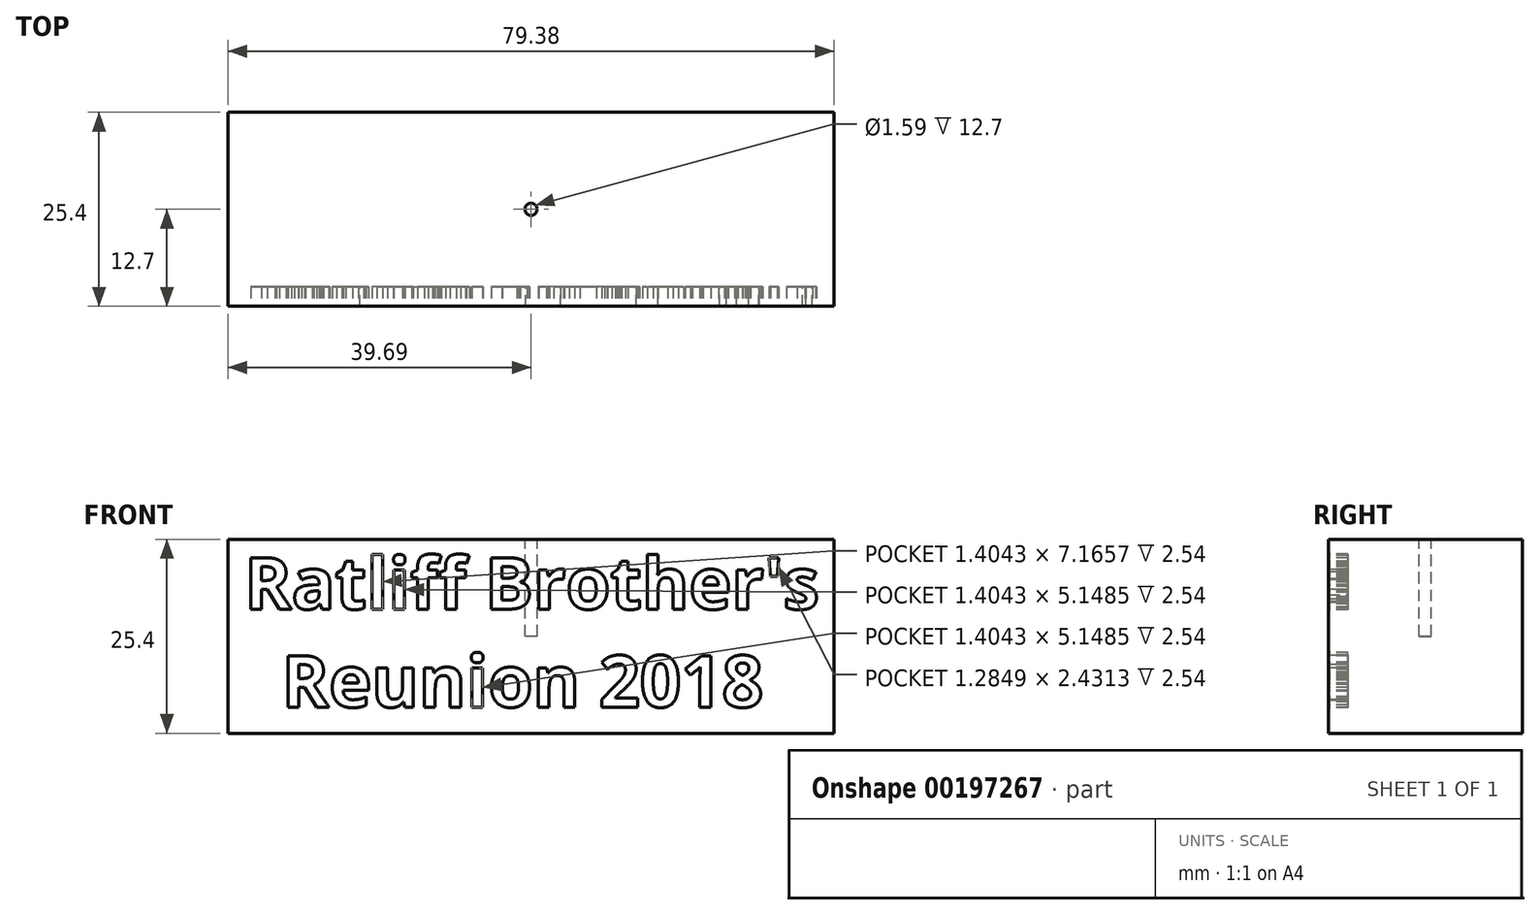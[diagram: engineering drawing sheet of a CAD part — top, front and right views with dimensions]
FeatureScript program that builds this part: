
annotation { "Feature Type Name" : "Feature", "Feature Type Description" : "" }
export const myFeature = defineFeature(function(context is Context, id is Id, definition is map)
    precondition{}
    {
        {
            var Q0;
            Q0=qCreatedBy(makeId("Top.planeOp"),FACE);
            var sketch = newSketch(context, id + "F0", { "sketchPlane" : qUnion([Q0])});
            skLineSegment(sketch, "E0.bottom", {"start": v(39.69, 12.7) * mm, "end": v(-39.69, 12.7) * mm});
            skLineSegment(sketch, "E0.top", {"start": v(39.69, -12.7) * mm, "end": v(-39.69, -12.7) * mm});
            skLineSegment(sketch, "E0.left", {"start": v(39.69, 12.7) * mm, "end": v(39.69, -12.7) * mm});
            skLineSegment(sketch, "E0.right", {"start": v(-39.69, 12.7) * mm, "end": v(-39.69, -12.7) * mm});
            skPoint(sketch, "E0.middle", {"position": v(0, 0) * mm});
            skSolve(sketch);
        }
        {
            var Q0;
            Q0=makeQuery(id+"F0.imprint","IMPRINT",FACE,{"disambiguationData":[TD([[makeQuery(id+"F0.imprint","IMPRINT",EDGE,{"derivedFrom":sQuery(id+"F0.wireOp",EDGE,"E0.bottom")}),1.0]])]});
            extrude(context, id + "F1", {"entities" : qUnion([Q0]), "endBound" : BoundingType.SYMMETRIC, "depth" : 25.4 * mm});
        }
        {
            var Q0;
            Q0=makeQuery(id+"F1.opExtrude","SWEPT_FACE",FACE,{"disambiguationData":[OSD([sQuery(id+"F0.wireOp",EDGE,"E0.top")])]});
            var sketch = newSketch(context, id + "F2", { "sketchPlane" : qUnion([Q0])});
            skText(sketch, "E1", { "text": "Ratliff Brother\'s\n  Reunion 2018", "fontName": "OpenSans-Bold.ttf"});
            const initialGuessF2  = {"E1": [-0.03758, 0.00356, 1, 0, 0.00679]};
            skSetInitialGuess(sketch, initialGuessF2);
            skSolve(sketch);
        }
        {
            var Q0;
            Q0 = qSketchRegion(id + "F2", true);
            extrude(context, id + "F3", {"entities" : qUnion([Q0]), "operationType" : NewBodyOperationType.REMOVE, "oppositeDirection" : true, "offsetDistance" : 25.4 * mm, "depth" : 2.54 * mm});
        }
        {
            var Q0;
            Q0=makeQuery(id+"F1.opExtrude","CAP_FACE",FACE,{"disambiguationData":[OSD([sQuery(id+"F0.wireOp",EDGE,"E0.bottom"),sQuery(id+"F0.wireOp",EDGE,"E0.top"),sQuery(id+"F0.wireOp",EDGE,"E0.left"),sQuery(id+"F0.wireOp",EDGE,"E0.right")])],"isStart":false});
            var sketch = newSketch(context, id + "F4", { "sketchPlane" : qUnion([Q0])});
            skCircle(sketch, "E2", {"center": v(0, 0) * mm, "radius": 0.8 * mm});
            skSolve(sketch);
        }
        {
            var Q0;
            Q0=makeQuery(id+"F4.imprint","IMPRINT",FACE,{"disambiguationData":[TD([[makeQuery(id+"F4.imprint","IMPRINT",EDGE,{"derivedFrom":sQuery(id+"F4.wireOp",EDGE,"E2")}),1.0]])]});
            extrude(context, id + "F5", {"entities" : qUnion([Q0]), "operationType" : NewBodyOperationType.REMOVE, "oppositeDirection" : true, "depth" : 12.7 * mm});
        }
    });
